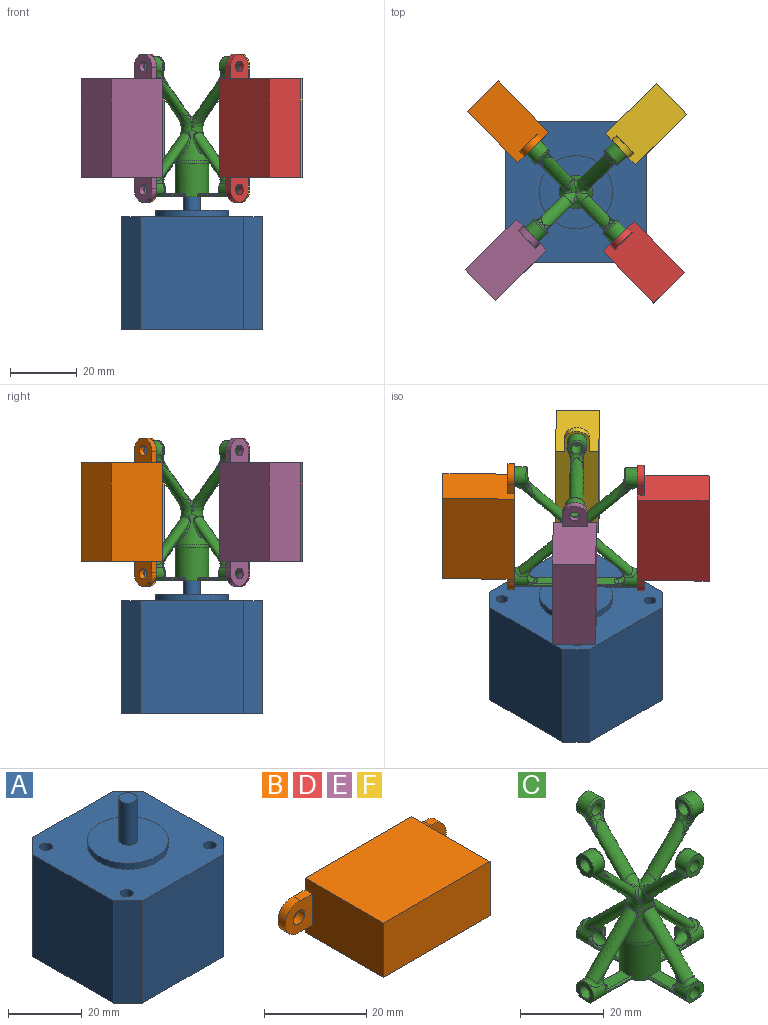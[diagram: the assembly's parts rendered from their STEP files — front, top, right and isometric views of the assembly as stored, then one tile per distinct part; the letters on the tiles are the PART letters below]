
ASSEMBLY  parts=6 mates=5
PART A: 22 faces, bbox 42.3x42.3x50 mm
  f0: plane 42.3x42.3mm, normal (0,0,1), area 1306.8mm2, adj f1,f2,f3,f4,f6,f10,f11,f12
  f1: plane 34x31mm, normal (0,-1,0), area 1054mm2, adj f0,f5,f10,f11
  f2: plane 34x31mm, normal (1,0,0), area 1054mm2, adj f0,f5,f11,f13
  f3: plane 34x31mm, normal (0,1,0), area 1054mm2, adj f0,f5,f12,f13
  f4: plane 34x31mm, normal (-1,0,0), area 1054mm2, adj f0,f5,f10,f12
  f5: plane 42.3x42.3mm, normal (0,0,-1), area 1725.4mm2, adj f1,f2,f3,f4,f10,f11,f12,f13
  f6: cylinder r=11mm len=22mm, axis (0,0,-1), area 138.2mm2, adj f0,f7
  f7: plane 22x22mm, normal (0,0,1), area 360.5mm2, adj f6,f8
  f8: cylinder r=2.5mm len=14mm, axis (0,0,-1), area 219.9mm2, adj f7,f9
  f9: plane 5x5mm, normal (0,0,1), area 19.6mm2, adj f8
  f10: plane 34x5.65mm, normal (-0.71,-0.71,0), area 271.7mm2, adj f0,f1,f4,f5
  f11: plane 34x5.65mm, normal (0.71,-0.71,0), area 271.7mm2, adj f0,f1,f2,f5
  f12: plane 34x5.65mm, normal (-0.71,0.71,0), area 271.7mm2, adj f0,f3,f4,f5
  f13: plane 34x5.65mm, normal (0.71,0.71,0), area 271.7mm2, adj f0,f2,f3,f5
  f14: cylinder r=1.75mm len=4.5mm, axis (0,0,1), area 49.5mm2, adj f0,f15
  f15: plane 3.5x3.5mm, normal (0,0,1), area 9.6mm2, adj f14
  f16: cylinder r=1.75mm len=4.5mm, axis (0,0,1), area 49.5mm2, adj f0,f17
  f17: plane 3.5x3.5mm, normal (0,0,1), area 9.6mm2, adj f16
  f18: cylinder r=1.75mm len=4.5mm, axis (0,0,1), area 49.5mm2, adj f0,f19
  f19: plane 3.5x3.5mm, normal (0,0,1), area 9.6mm2, adj f18
  f20: cylinder r=1.75mm len=4.5mm, axis (0,0,1), area 49.5mm2, adj f0,f21
  f21: plane 3.5x3.5mm, normal (0,0,1), area 9.6mm2, adj f20
PART B: 16 faces, bbox 44.5x21.6x13 mm
  f0: plane 21.6x13mm, normal (1,0,0), area 265.9mm2, adj f2,f3,f4,f5,f12,f14,f15
  f1: plane 21.6x13mm, normal (-1,0,0), area 265.9mm2, adj f2,f3,f4,f5,f8,f9,f10
  f2: plane 29.5x21.6mm, normal (0,0,-1), area 637.2mm2, adj f0,f1,f4,f5
  f3: plane 29.5x21.6mm, normal (0,0,1), area 637.2mm2, adj f0,f1,f4,f5
  f4: plane 29.5x13mm, normal (0,-1,0), area 383.5mm2, adj f0,f1,f2,f3
  f5: plane 44.5x13mm, normal (0,1,0), area 467.5mm2, adj f0,f1,f2,f3,f6,f7,f9,f10
  f6: cylinder r=3.75mm len=7.5mm, axis (0,1,0), area 25.4mm2, adj f5,f8,f9,f10
  f7: cylinder r=1.6mm len=3.2mm, axis (0,1,0), area 20.1mm2, adj f5,f8
  f8: plane 7.5x7.5mm, normal (0,-1,0), area 42mm2, adj f1,f6,f7,f9,f10
  f9: plane 3.3x2mm, normal (0,0,-1), area 6.6mm2, adj f1,f5,f6,f8
  f10: plane 3.3x2mm, normal (0,0,1), area 6.6mm2, adj f1,f5,f6,f8
  f11: cylinder r=3.75mm len=7.5mm, axis (0,1,0), area 25.4mm2, adj f5,f12,f14,f15
  f12: plane 3.3x2mm, normal (0,0,1), area 6.6mm2, adj f0,f5,f11,f15
  f13: cylinder r=1.6mm len=3.2mm, axis (0,1,0), area 20.1mm2, adj f5,f15
  f14: plane 3.3x2mm, normal (0,0,-1), area 6.6mm2, adj f0,f5,f11,f15
  f15: plane 7.5x7.5mm, normal (0,-1,0), area 42mm2, adj f0,f11,f12,f13,f14
PART C: 199 faces, bbox 44.4x44.4x59.2 mm
  f0: bspline ~5.01x4.22mm, area 14.1mm2, adj f1,f14,f192,f196
  f1: bspline ~5.83x4.16mm, area 12.9mm2, adj f0,f2,f14,f189,f197
  f2: bspline ~5.2x3.3mm, area 13.5mm2, adj f1,f13,f38,f186,f198
  f3: plane 1.47x0.76mm, normal (-1,0,0), area 0.6mm2, adj f16,f22,f25,f26
  f4: plane 7.81x3.36mm, normal (0,0,1), area 23.4mm2, adj f8,f23,f24,f26,f27,f30,f33
  f5: plane 8.92x0.56mm, normal (0,-1,0), area 3.1mm2, adj f8,f28,f33,f34,f37
  f6: plane 8.92x0.56mm, normal (0,1,0), area 3.1mm2, adj f8,f29,f30,f31,f36
  f7: cylinder r=2.9mm len=10mm, axis (0,0,-1), area 182.2mm2, adj f10,f11
  f8: cylinder r=5mm len=10.17mm, axis (0,0,-1), area 304mm2, adj f4,f5,f6,f10,f12,f30,f33,f36
  f9: bspline ~17.9x13.95mm, area 172.7mm2, adj f25,f38,f39
  f10: plane 37x37mm, normal (0,0,-1), area 233.4mm2, adj f7,f8,f15,f36,f37,f63,f84,f85
  f11: plane 5.8x5.8mm, normal (0,0,-1), area 26.4mm2, adj f7
  f12: torus R=2mm, axis (0,0,1), area 24mm2, adj f8,f13
  f13: torus R=62.94mm, axis (0,0,-1), area 125.5mm2, adj f2,f12,f38,f54,f56,f86,f101,f131
  f14: bspline ~16.86x12.91mm, area 160.3mm2, adj f0,f1,f40,f41,f42,f43,f44,f45
  f15: plane 5.92x5.14mm, normal (1,0,0), area 15.8mm2, adj f10,f16,f22,f36,f37
  f16: cylinder r=2.96mm len=5.92mm, axis (1,0,0), area 27.6mm2, adj f3,f15,f17,f25,f26,f27,f28,f29
  f17: plane 1.47x0.76mm, normal (-1,0,0), area 0.6mm2, adj f16,f22,f25,f27
  f18: cylinder r=2.96mm len=5.92mm, axis (1,0,0), area 46.4mm2, adj f20,f40,f42,f48
  f19: plane 4.92x3.78mm, normal (-1,0,0), area 6.8mm2, adj f21,f43,f45,f47,f48,f49
  f20: plane 5.99x5.99mm, normal (1,0,0), area 18.4mm2, adj f18,f21,f41
  f21: cylinder r=1.7mm len=4mm, axis (1,0,0), area 42.7mm2, adj f19,f20,f44
  f22: cylinder r=1.7mm len=5.92mm, axis (1,0,0), area 50.2mm2, adj f3,f15,f17,f24,f25,f26,f27
  f23: plane 0.32x0.08mm, normal (0.71,0,0.71), area 0mm2, adj f4,f24
  f24: bspline ~3.13x1.18mm, area 2.6mm2, adj f4,f22,f23,f26,f27
  f25: bspline ~8.73x4.32mm, area 9.6mm2, adj f3,f9,f16,f17,f22,f39
  f26: cylinder r=2mm len=2mm, axis (0,1,0), area 1.6mm2, adj f3,f4,f16,f22,f24,f34,f35
  f27: cylinder r=2mm len=2mm, axis (0,1,0), area 1.6mm2, adj f4,f16,f17,f22,f24,f31,f32
  f28: cylinder r=1mm len=2.5mm, axis (0,0,1), area 1.6mm2, adj f5,f16,f35,f37
  f29: cylinder r=1mm len=2.5mm, axis (0,0,-1), area 1.6mm2, adj f6,f16,f32,f36
  f30: plane 7.92x0.34mm, normal (0,0.71,0.71), area 3.7mm2, adj f4,f6,f8,f31
  f31: cone r=2.33mm half-angle=45deg, axis (0,1,0), area 0.5mm2, adj f6,f27,f30,f32
  f32: bspline ~1.96x1.23mm, area 0.7mm2, adj f27,f29,f31
  f33: plane 7.92x0.34mm, normal (0,-0.71,0.71), area 3.7mm2, adj f4,f5,f8,f34
  f34: cone r=2.33mm half-angle=45deg, axis (0,-1,0), area 0.5mm2, adj f5,f26,f33,f35
  f35: bspline ~1.96x1.23mm, area 0.7mm2, adj f26,f28,f34
  f36: plane 14.25x1.41mm, normal (0,0.71,-0.71), area 11mm2, adj f6,f8,f10,f15,f16,f29
  f37: plane 14.25x1.41mm, normal (0,-0.71,-0.71), area 11mm2, adj f5,f8,f10,f15,f16,f28
  f38: bspline ~6.56x4.4mm, area 11.4mm2, adj f2,f9,f13
  f39: bspline ~7.31x4.78mm, area 16.8mm2, adj f9,f16,f25
  f40: bspline ~8.08x4.52mm, area 6.3mm2, adj f14,f18,f41,f49,f50
  f41: bspline ~4.4x2.42mm, area 10.2mm2, adj f14,f20,f40,f42
  f42: bspline ~7.85x4.33mm, area 6.3mm2, adj f14,f18,f41,f46,f47
  f43: bspline ~5.24x4.37mm, area 2.8mm2, adj f14,f19,f44,f50
  f44: bspline ~2.76x2.06mm, area 3mm2, adj f14,f21,f43,f45
  f45: bspline ~5.6x4.61mm, area 2.9mm2, adj f14,f19,f44,f46
  f46: bspline ~4.91x2.74mm, area 1.5mm2, adj f42,f45,f47
  f47: bspline ~0.7x0.68mm, area 0.1mm2, adj f19,f42,f46,f48
  f48: torus R=2.46mm, axis (1,0,0), area 9mm2, adj f18,f19,f47,f49
  f49: bspline ~0.71x0.69mm, area 0.1mm2, adj f19,f40,f48,f50
  f50: bspline ~4.91x2.74mm, area 1.5mm2, adj f40,f43,f49
  f51: bspline ~5.01x4.22mm, area 14.1mm2, adj f53,f62,f194,f196
  f52: bspline ~5.01x4.22mm, area 14.1mm2, adj f55,f149,f192,f193
  f53: bspline ~5.83x4.16mm, area 12.9mm2, adj f51,f54,f62,f191,f197
  f54: bspline ~5.2x3.3mm, area 13.5mm2, adj f13,f53,f86,f188,f198
  f55: bspline ~5.83x4.16mm, area 12.9mm2, adj f52,f56,f149,f189,f190
  f56: bspline ~5.2x3.3mm, area 13.5mm2, adj f13,f55,f173,f186,f187
  f57: plane 1.47x0.76mm, normal (0,-1,0), area 0.6mm2, adj f64,f70,f73,f74
  f58: plane 7.81x3.36mm, normal (0,0,1), area 23.4mm2, adj f8,f71,f72,f74,f75,f78,f81
  f59: plane 8.92x0.56mm, normal (1,0,0), area 3.1mm2, adj f8,f76,f81,f82,f85
  f60: plane 8.92x0.56mm, normal (-1,0,0), area 3.1mm2, adj f8,f77,f78,f79,f84
  f61: bspline ~17.9x13.95mm, area 172.7mm2, adj f73,f86,f87
  f62: bspline ~16.86x12.91mm, area 160.3mm2, adj f51,f53,f88,f89,f90,f91,f92,f93
  f63: plane 5.92x5.14mm, normal (0,1,0), area 15.8mm2, adj f10,f64,f70,f84,f85
  f64: cylinder r=2.96mm len=5.92mm, axis (0,1,0), area 27.6mm2, adj f57,f63,f65,f73,f74,f75,f76,f77
  f65: plane 1.47x0.76mm, normal (0,-1,0), area 0.6mm2, adj f64,f70,f73,f75
  f66: cylinder r=2.96mm len=5.92mm, axis (0,1,0), area 46.4mm2, adj f68,f88,f90,f96
  f67: plane 4.92x3.78mm, normal (0,-1,0), area 6.8mm2, adj f69,f91,f93,f95,f96,f97
  f68: plane 5.99x5.99mm, normal (0,1,0), area 18.4mm2, adj f66,f69,f89
  f69: cylinder r=1.7mm len=4mm, axis (0,1,0), area 42.7mm2, adj f67,f68,f92
  f70: cylinder r=1.7mm len=5.92mm, axis (0,1,0), area 50.2mm2, adj f57,f63,f65,f72,f73,f74,f75
  f71: plane 0.32x0.08mm, normal (0,0.71,0.71), area 0mm2, adj f58,f72
  f72: bspline ~3.13x1.18mm, area 2.6mm2, adj f58,f70,f71,f74,f75
  f73: bspline ~8.73x4.32mm, area 9.6mm2, adj f57,f61,f64,f65,f70,f87
  f74: cylinder r=2mm len=2mm, axis (-1,0,0), area 1.6mm2, adj f57,f58,f64,f70,f72,f82,f83
  f75: cylinder r=2mm len=2mm, axis (-1,0,0), area 1.6mm2, adj f58,f64,f65,f70,f72,f79,f80
  f76: cylinder r=1mm len=2.5mm, axis (0,0,1), area 1.6mm2, adj f59,f64,f83,f85
  f77: cylinder r=1mm len=2.5mm, axis (0,0,-1), area 1.6mm2, adj f60,f64,f80,f84
  f78: plane 7.92x0.34mm, normal (-0.71,0,0.71), area 3.7mm2, adj f8,f58,f60,f79
  f79: cone r=2.33mm half-angle=45deg, axis (-1,0,0), area 0.5mm2, adj f60,f75,f78,f80
  f80: bspline ~1.96x1.23mm, area 0.7mm2, adj f75,f77,f79
  f81: plane 7.92x0.34mm, normal (0.71,0,0.71), area 3.7mm2, adj f8,f58,f59,f82
  f82: cone r=2.33mm half-angle=45deg, axis (1,0,0), area 0.5mm2, adj f59,f74,f81,f83
  f83: bspline ~1.96x1.23mm, area 0.7mm2, adj f74,f76,f82
  f84: plane 14.25x1.41mm, normal (-0.71,0,-0.71), area 11mm2, adj f8,f10,f60,f63,f64,f77
  f85: plane 14.25x1.41mm, normal (0.71,0,-0.71), area 11mm2, adj f8,f10,f59,f63,f64,f76
  f86: bspline ~6.56x4.4mm, area 11.4mm2, adj f13,f54,f61
  f87: bspline ~7.31x4.78mm, area 16.8mm2, adj f61,f64,f73
  f88: bspline ~8.08x4.52mm, area 6.3mm2, adj f62,f66,f89,f97,f98
  f89: bspline ~4.4x2.42mm, area 10.2mm2, adj f62,f68,f88,f90
  f90: bspline ~7.85x4.33mm, area 6.3mm2, adj f62,f66,f89,f94,f95
  f91: bspline ~5.24x4.37mm, area 2.8mm2, adj f62,f67,f92,f98
  f92: bspline ~2.76x2.06mm, area 3mm2, adj f62,f69,f91,f93
  f93: bspline ~5.6x4.61mm, area 2.9mm2, adj f62,f67,f92,f94
  f94: bspline ~4.91x2.74mm, area 1.5mm2, adj f90,f93,f95
  f95: bspline ~0.7x0.68mm, area 0.1mm2, adj f67,f90,f94,f96
  f96: torus R=2.46mm, axis (0,1,0), area 9mm2, adj f66,f67,f95,f97
  f97: bspline ~0.71x0.69mm, area 0.1mm2, adj f67,f88,f96,f98
  f98: bspline ~4.91x2.74mm, area 1.5mm2, adj f88,f91,f97
  f99: bspline ~5.01x4.22mm, area 14.1mm2, adj f100,f107,f193,f194
  f100: bspline ~5.83x4.16mm, area 12.9mm2, adj f99,f101,f107,f190,f191
  f101: bspline ~5.2x3.3mm, area 13.5mm2, adj f13,f100,f131,f187,f188
  f102: plane 1.47x0.76mm, normal (1,0,0), area 0.6mm2, adj f109,f115,f118,f119
  f103: plane 7.81x3.36mm, normal (0,0,1), area 23.4mm2, adj f8,f116,f117,f119,f120,f123,f126
  f104: plane 8.92x0.56mm, normal (0,1,0), area 3.1mm2, adj f8,f121,f126,f127,f130
  f105: plane 8.92x0.56mm, normal (0,-1,0), area 3.1mm2, adj f8,f122,f123,f124,f129
  f106: bspline ~17.9x13.95mm, area 172.7mm2, adj f118,f131,f132
  f107: bspline ~16.86x12.91mm, area 160.3mm2, adj f99,f100,f133,f134,f135,f136,f137,f138
  f108: plane 5.92x5.14mm, normal (-1,0,0), area 15.8mm2, adj f10,f109,f115,f129,f130
  f109: cylinder r=2.96mm len=5.92mm, axis (-1,0,0), area 27.6mm2, adj f102,f108,f110,f118,f119,f120,f121,f122
  f110: plane 1.47x0.76mm, normal (1,0,0), area 0.6mm2, adj f109,f115,f118,f120
  f111: cylinder r=2.96mm len=5.92mm, axis (-1,0,0), area 46.4mm2, adj f113,f133,f135,f141
  f112: plane 4.92x3.78mm, normal (1,0,0), area 6.8mm2, adj f114,f136,f138,f140,f141,f142
  f113: plane 5.99x5.99mm, normal (-1,0,0), area 18.4mm2, adj f111,f114,f134
  f114: cylinder r=1.7mm len=4mm, axis (-1,0,0), area 42.7mm2, adj f112,f113,f137
  f115: cylinder r=1.7mm len=5.92mm, axis (-1,0,0), area 50.2mm2, adj f102,f108,f110,f117,f118,f119,f120
  f116: plane 0.32x0.08mm, normal (-0.71,0,0.71), area 0mm2, adj f103,f117
  f117: bspline ~3.13x1.18mm, area 2.6mm2, adj f103,f115,f116,f119,f120
  f118: bspline ~8.73x4.32mm, area 9.6mm2, adj f102,f106,f109,f110,f115,f132
  f119: cylinder r=2mm len=2mm, axis (0,-1,0), area 1.6mm2, adj f102,f103,f109,f115,f117,f127,f128
  f120: cylinder r=2mm len=2mm, axis (0,-1,0), area 1.6mm2, adj f103,f109,f110,f115,f117,f124,f125
  f121: cylinder r=1mm len=2.5mm, axis (0,0,1), area 1.6mm2, adj f104,f109,f128,f130
  f122: cylinder r=1mm len=2.5mm, axis (0,0,-1), area 1.6mm2, adj f105,f109,f125,f129
  f123: plane 7.92x0.34mm, normal (0,-0.71,0.71), area 3.7mm2, adj f8,f103,f105,f124
  f124: cone r=2.33mm half-angle=45deg, axis (0,-1,0), area 0.5mm2, adj f105,f120,f123,f125
  f125: bspline ~1.96x1.23mm, area 0.7mm2, adj f120,f122,f124
  f126: plane 7.92x0.34mm, normal (0,0.71,0.71), area 3.7mm2, adj f8,f103,f104,f127
  f127: cone r=2.33mm half-angle=45deg, axis (0,1,0), area 0.5mm2, adj f104,f119,f126,f128
  f128: bspline ~1.96x1.23mm, area 0.7mm2, adj f119,f121,f127
  f129: plane 14.25x1.41mm, normal (0,-0.71,-0.71), area 11mm2, adj f8,f10,f105,f108,f109,f122
  f130: plane 14.25x1.41mm, normal (0,0.71,-0.71), area 11mm2, adj f8,f10,f104,f108,f109,f121
  f131: bspline ~6.56x4.4mm, area 11.4mm2, adj f13,f101,f106
  f132: bspline ~7.31x4.78mm, area 16.8mm2, adj f106,f109,f118
  f133: bspline ~8.08x4.52mm, area 6.3mm2, adj f107,f111,f134,f142,f143
  f134: bspline ~4.4x2.42mm, area 10.2mm2, adj f107,f113,f133,f135
  f135: bspline ~7.85x4.33mm, area 6.3mm2, adj f107,f111,f134,f139,f140
  f136: bspline ~5.24x4.37mm, area 2.8mm2, adj f107,f112,f137,f143
  f137: bspline ~2.76x2.06mm, area 3mm2, adj f107,f114,f136,f138
  f138: bspline ~5.6x4.61mm, area 2.9mm2, adj f107,f112,f137,f139
  f139: bspline ~4.91x2.74mm, area 1.5mm2, adj f135,f138,f140
  f140: bspline ~0.7x0.68mm, area 0.1mm2, adj f112,f135,f139,f141
  f141: torus R=2.46mm, axis (-1,0,0), area 9mm2, adj f111,f112,f140,f142
  f142: bspline ~0.71x0.69mm, area 0.1mm2, adj f112,f133,f141,f143
  f143: bspline ~4.91x2.74mm, area 1.5mm2, adj f133,f136,f142
  f144: plane 1.47x0.76mm, normal (0,1,0), area 0.6mm2, adj f151,f157,f160,f161
  f145: plane 7.81x3.36mm, normal (0,0,1), area 23.4mm2, adj f8,f158,f159,f161,f162,f165,f168
  f146: plane 8.92x0.56mm, normal (-1,0,0), area 3.1mm2, adj f8,f163,f168,f169,f172
  f147: plane 8.92x0.56mm, normal (1,0,0), area 3.1mm2, adj f8,f164,f165,f166,f171
  f148: bspline ~17.9x13.95mm, area 172.7mm2, adj f160,f173,f174
  f149: bspline ~16.86x12.91mm, area 160.3mm2, adj f52,f55,f175,f176,f177,f178,f179,f180
  f150: plane 5.92x5.14mm, normal (0,-1,0), area 15.8mm2, adj f10,f151,f157,f171,f172
  f151: cylinder r=2.96mm len=5.92mm, axis (0,-1,0), area 27.6mm2, adj f144,f150,f152,f160,f161,f162,f163,f164
  f152: plane 1.47x0.76mm, normal (0,1,0), area 0.6mm2, adj f151,f157,f160,f162
  f153: cylinder r=2.96mm len=5.92mm, axis (0,-1,0), area 46.4mm2, adj f155,f175,f177,f183
  f154: plane 4.92x3.78mm, normal (0,1,0), area 6.8mm2, adj f156,f178,f180,f182,f183,f184
  f155: plane 5.99x5.99mm, normal (0,-1,0), area 18.4mm2, adj f153,f156,f176
  f156: cylinder r=1.7mm len=4mm, axis (0,-1,0), area 42.7mm2, adj f154,f155,f179
  f157: cylinder r=1.7mm len=5.92mm, axis (0,-1,0), area 50.2mm2, adj f144,f150,f152,f159,f160,f161,f162
  f158: plane 0.32x0.08mm, normal (0,-0.71,0.71), area 0mm2, adj f145,f159
  f159: bspline ~3.13x1.18mm, area 2.6mm2, adj f145,f157,f158,f161,f162
  f160: bspline ~8.73x4.32mm, area 9.6mm2, adj f144,f148,f151,f152,f157,f174
  f161: cylinder r=2mm len=2mm, axis (1,0,0), area 1.6mm2, adj f144,f145,f151,f157,f159,f169,f170
  f162: cylinder r=2mm len=2mm, axis (1,0,0), area 1.6mm2, adj f145,f151,f152,f157,f159,f166,f167
  f163: cylinder r=1mm len=2.5mm, axis (0,0,1), area 1.6mm2, adj f146,f151,f170,f172
  f164: cylinder r=1mm len=2.5mm, axis (0,0,-1), area 1.6mm2, adj f147,f151,f167,f171
  f165: plane 7.92x0.34mm, normal (0.71,0,0.71), area 3.7mm2, adj f8,f145,f147,f166
  f166: cone r=2.33mm half-angle=45deg, axis (1,0,0), area 0.5mm2, adj f147,f162,f165,f167
  f167: bspline ~1.96x1.23mm, area 0.7mm2, adj f162,f164,f166
  f168: plane 7.92x0.34mm, normal (-0.71,0,0.71), area 3.7mm2, adj f8,f145,f146,f169
  f169: cone r=2.33mm half-angle=45deg, axis (-1,0,0), area 0.5mm2, adj f146,f161,f168,f170
  f170: bspline ~1.96x1.23mm, area 0.7mm2, adj f161,f163,f169
  f171: plane 14.25x1.41mm, normal (0.71,0,-0.71), area 11mm2, adj f8,f10,f147,f150,f151,f164
  f172: plane 14.25x1.41mm, normal (-0.71,0,-0.71), area 11mm2, adj f8,f10,f146,f150,f151,f163
  f173: bspline ~6.56x4.4mm, area 11.4mm2, adj f13,f56,f148
  f174: bspline ~7.31x4.78mm, area 16.8mm2, adj f148,f151,f160
  f175: bspline ~8.08x4.52mm, area 6.3mm2, adj f149,f153,f176,f184,f185
  f176: bspline ~4.4x2.42mm, area 10.2mm2, adj f149,f155,f175,f177
  f177: bspline ~7.85x4.33mm, area 6.3mm2, adj f149,f153,f176,f181,f182
  f178: bspline ~5.24x4.37mm, area 2.8mm2, adj f149,f154,f179,f185
  f179: bspline ~2.76x2.06mm, area 3mm2, adj f149,f156,f178,f180
  f180: bspline ~5.6x4.61mm, area 2.9mm2, adj f149,f154,f179,f181
  f181: bspline ~4.91x2.74mm, area 1.5mm2, adj f177,f180,f182
  f182: bspline ~0.7x0.68mm, area 0.1mm2, adj f154,f177,f181,f183
  f183: torus R=2.46mm, axis (0,-1,0), area 9mm2, adj f153,f154,f182,f184
  f184: bspline ~0.71x0.69mm, area 0.1mm2, adj f154,f175,f183,f185
  f185: bspline ~4.91x2.74mm, area 1.5mm2, adj f175,f178,f184
  f186: bspline ~1.78x0.19mm, area 0mm2, adj f2,f56,f189
  f187: bspline ~1.78x0.19mm, area 0mm2, adj f56,f101,f190
  f188: bspline ~1.78x0.19mm, area 0mm2, adj f54,f101,f191
  f189: bspline ~1.1x0.25mm, area 0.2mm2, adj f1,f55,f186,f192
  f190: bspline ~1.1x0.25mm, area 0.2mm2, adj f55,f100,f187,f193
  f191: bspline ~1.1x0.25mm, area 0.2mm2, adj f53,f100,f188,f194
  f192: bspline ~2.9x2.74mm, area 3.1mm2, adj f0,f52,f189,f195
  f193: bspline ~3.02x2.9mm, area 3.1mm2, adj f52,f99,f190,f195
  f194: bspline ~3.02x2.9mm, area 3.1mm2, adj f51,f99,f191,f195
  f195: sphere r=0.5mm, area 0.1mm2, adj f192,f193,f194,f196
  f196: bspline ~3.19x2.91mm, area 3.1mm2, adj f0,f51,f195,f197
  f197: bspline ~1.1x0.25mm, area 0.2mm2, adj f1,f53,f196,f198
  f198: bspline ~1.78x0.19mm, area 0mm2, adj f2,f54,f197
PART D: same geometry as B
PART E: same geometry as B
PART F: same geometry as B
PLACE A rot(axis=(0,0,1),90deg) t=(0,0,0)mm
PLACE B rot(axis=(-0.68,-0.28,-0.68),149.2deg) t=(-12.87,13.29,60.68)mm
PLACE C rot(axis=(0,0,-1),45.9deg) t=(0,0,40)mm
PLACE D rot(axis=(0.35,-0.87,0.35),98.1deg) t=(12.87,-13.29,60.68)mm
PLACE E rot(axis=(-0.36,-0.86,-0.36),98.8deg) t=(-13.29,-12.87,60.68)mm
PLACE F rot(axis=(0.68,-0.29,0.68),148deg) t=(13.29,12.87,60.68)mm
MATE fastened F.f11 <-> C.f66  axis (-0.72,-0.7,0) through (13.29,12.87,79.18)mm
MATE fastened E.f11 <-> C.f153  axis (0.72,0.7,0) through (-13.29,-12.87,79.18)mm
MATE fastened D.f11 <-> C.f18  axis (-0.7,0.72,0) through (12.87,-13.29,79.18)mm
MATE revolute C.f7 <-> A.f6  axis (0,0,-1) through (0,0,50)mm
MATE fastened B.f11 <-> C.f111  axis (0.7,-0.72,0) through (-12.87,13.29,79.18)mm
